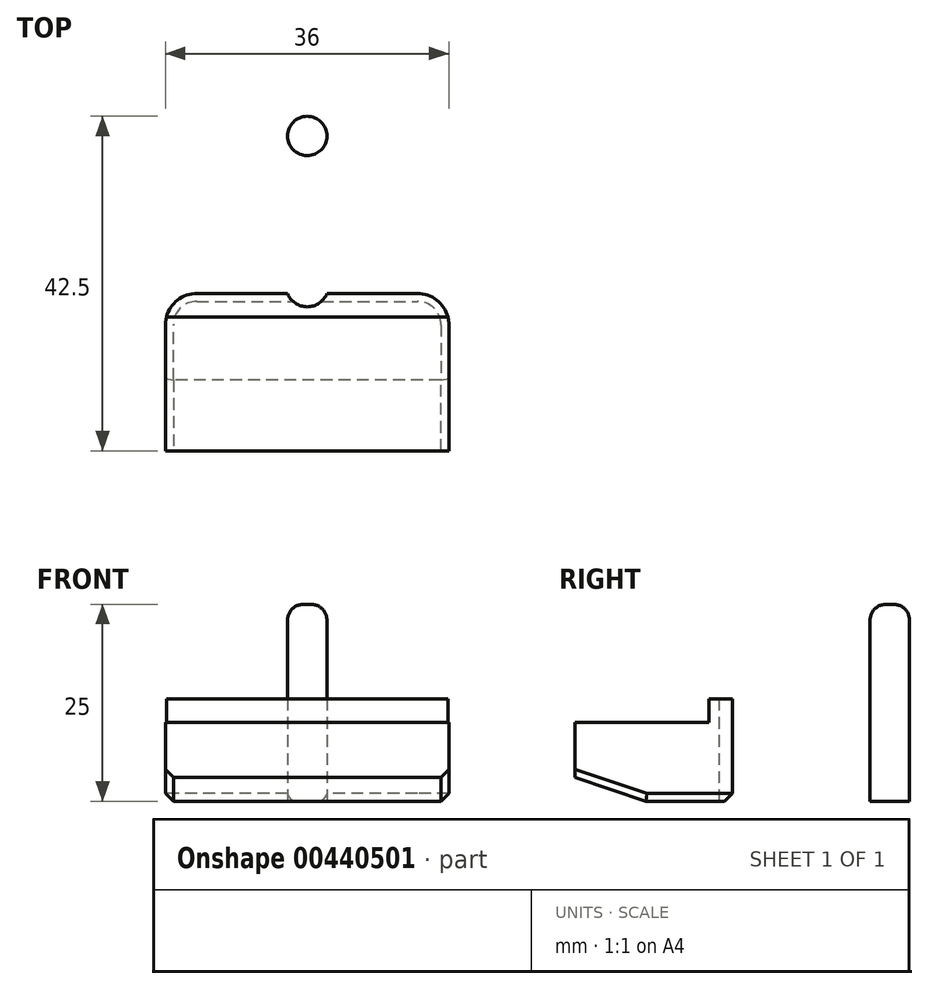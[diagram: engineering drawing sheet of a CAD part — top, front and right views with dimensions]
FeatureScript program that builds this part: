
annotation { "Feature Type Name" : "Feature", "Feature Type Description" : "" }
export const myFeature = defineFeature(function(context is Context, id is Id, definition is map)
    precondition{}
    {
        {
            var Q0;
            Q0=qCreatedBy(makeId("Top.planeOp"),FACE);
            var sketch = newSketch(context, id + "F0", { "sketchPlane" : qUnion([Q0])});
            skLineSegment(sketch, "E0.bottom", {"start": v(-18, 0) * mm, "end": v(18, 0) * mm});
            skLineSegment(sketch, "E0.top", {"start": v(-18, 20) * mm, "end": v(18, 20) * mm});
            skLineSegment(sketch, "E0.left", {"start": v(-18, 0) * mm, "end": v(-18, 20) * mm});
            skLineSegment(sketch, "E0.right", {"start": v(18, 0) * mm, "end": v(18, 20) * mm});
            skLineSegment(sketch, "E1.bottom", {"start": v(-10, 20) * mm, "end": v(10, 20) * mm});
            skLineSegment(sketch, "E1.top", {"start": v(-10, 50) * mm, "end": v(10, 50) * mm});
            skLineSegment(sketch, "E1.left", {"start": v(-10, 20) * mm, "end": v(-10, 50) * mm});
            skLineSegment(sketch, "E1.right", {"start": v(10, 20) * mm, "end": v(10, 50) * mm});
            skPoint(sketch, "E2", {"position": v(0, 21) * mm});
            skPoint(sketch, "E2.positionSnap0", {"position": v(0, 20) * mm});
            skPoint(sketch, "E3", {"position": v(0, 40) * mm});
            skCircle(sketch, "E4", {"center": v(0, 40) * mm, "radius": 2.5 * mm});
            skSolve(sketch);
        }
        {
            var Q0;
            Q0=makeQuery(id+"F0.imprint","IMPRINT",FACE,{"disambiguationData":[TD([[makeQuery(id+"F0.imprint","IMPRINT",EDGE,{"derivedFrom":sQuery(id+"F0.wireOp",EDGE,"E0.bottom")}),1.0]])]});
            var Q1;
            Q1=makeQuery(id+"F0.imprint","IMPRINT",FACE,{"disambiguationData":[TD([[makeQuery(id+"F0.imprint","IMPRINT",EDGE,{"derivedFrom":sQuery(id+"F0.wireOp",EDGE,"E1.bottom")}),1.0]])]});
            var Q2;
            Q2=makeQuery(id+"F0.imprint","IMPRINT",FACE,{"disambiguationData":[TD([[makeQuery(id+"F0.imprint","IMPRINT",EDGE,{"derivedFrom":sQuery(id+"F0.wireOp",EDGE,"E4")}),1.0]])]});
            extrude(context, id + "F1", {"entities" : qUnion([Q0, Q1, Q2]), "depth" : 13 * mm});
        }
        {
            var Q0;
            Q0=makeQuery(id+"F1.opExtrude","CAP_FACE",FACE,{"disambiguationData":[OSD([sQuery(id+"F0.wireOp",EDGE,"E0.bottom"),sQuery(id+"F0.wireOp",EDGE,"E0.top"),sQuery(id+"F0.wireOp",EDGE,"E0.left"),sQuery(id+"F0.wireOp",EDGE,"E0.right"),sQuery(id+"F0.wireOp",EDGE,"E1.top"),sQuery(id+"F0.wireOp",EDGE,"E1.left"),sQuery(id+"F0.wireOp",EDGE,"E1.right")])],"isStart":false});
            var sketch = newSketch(context, id + "F2", { "sketchPlane" : qUnion([Q0])});
            skLineSegment(sketch, "E5.bottom", {"start": v(-18, 0) * mm, "end": v(18, 0) * mm});
            skLineSegment(sketch, "E5.top", {"start": v(-18, 17) * mm, "end": v(18, 17) * mm});
            skLineSegment(sketch, "E5.left", {"start": v(-18, 0) * mm, "end": v(-18, 17) * mm});
            skLineSegment(sketch, "E5.right", {"start": v(18, 0) * mm, "end": v(18, 17) * mm});
            skSolve(sketch);
        }
        {
            var Q0;
            Q0=makeQuery(id+"F2.imprint","IMPRINT",FACE,{"disambiguationData":[TD([[makeQuery(id+"F2.imprint","IMPRINT",EDGE,{"derivedFrom":sQuery(id+"F2.wireOp",EDGE,"E5.bottom")}),1.0]])]});
            extrude(context, id + "F3", {"entities" : qUnion([Q0]), "operationType" : NewBodyOperationType.REMOVE, "oppositeDirection" : true, "depth" : 3 * mm});
        }
        {
            var Q0;
            Q0=sQuery(id+"F0.wireOp",VERTEX,"E2");
            var Q1;
            Q1=makeQuery(id+"F1.opExtrude","SWEPT_BODY",BODY,{"disambiguationData":[OSD([sQuery(id+"F0.wireOp",EDGE,"E0.bottom"),sQuery(id+"F0.wireOp",EDGE,"E0.top"),sQuery(id+"F0.wireOp",EDGE,"E0.left"),sQuery(id+"F0.wireOp",EDGE,"E0.right"),sQuery(id+"F0.wireOp",EDGE,"E1.top"),sQuery(id+"F0.wireOp",EDGE,"E1.left"),sQuery(id+"F0.wireOp",EDGE,"E1.right")])]});
            hole(context, id + "F4", {"style" : HoleStyle.SIMPLE, "endStyle" : HoleEndStyle.THROUGH, "oppositeDirection" : true, "holeDiameter" : 5.4 * mm, "isTappedThrough" : true, "tappedDepth" : 12 * mm, "tapClearance" : 3, "locations" : qUnion([Q0]), "scope" : qUnion([Q1])});
        }
        {
            var Q0;
            Q0=makeQuery(id+"F0.imprint","IMPRINT",FACE,{"disambiguationData":[TD([[makeQuery(id+"F0.imprint","IMPRINT",EDGE,{"derivedFrom":sQuery(id+"F0.wireOp",EDGE,"E4")}),1.0]])]});
            extrude(context, id + "F5", {"entities" : qUnion([Q0]), "operationType" : NewBodyOperationType.ADD, "depth" : 25 * mm});
        }
        {
            var Q0;
            Q0=makeQuery(id+"F5.opExtrude","CAP_EDGE",EDGE,{"disambiguationData":[OSD([sQuery(id+"F0.wireOp",EDGE,"E4")])],"isStart":false});
            fillet(context, id + "F6", {"entities" : qUnion([Q0]), "radius" : 2 * mm, "tangentPropagation" : true, "allowEdgeOverflow" : false});
        }
        {
            var Q0;
            Q0=makeQuery(id+"F1.opExtrude","SWEPT_EDGE",EDGE,{"disambiguationData":[OSD([sQuery(id+"F0.wireOp",EDGE,"E0.top"),sQuery(id+"F0.wireOp",EDGE,"E0.left")])]});
            var Q1;
            Q1=makeQuery(id+"F1.opExtrude","SWEPT_EDGE",EDGE,{"disambiguationData":[OSD([sQuery(id+"F0.wireOp",EDGE,"E0.top"),sQuery(id+"F0.wireOp",EDGE,"E0.right")])]});
            var Q2;
            Q2=makeQuery(id+"F1.opExtrude","SWEPT_EDGE",EDGE,{"disambiguationData":[OSD([sQuery(id+"F0.wireOp",EDGE,"E0.top"),sQuery(id+"F0.wireOp",EDGE,"E1.bottom"),sQuery(id+"F0.wireOp",EDGE,"E1.left")])]});
            var Q3;
            Q3=makeQuery(id+"F1.opExtrude","SWEPT_EDGE",EDGE,{"disambiguationData":[OSD([sQuery(id+"F0.wireOp",EDGE,"E0.top"),sQuery(id+"F0.wireOp",EDGE,"E1.bottom"),sQuery(id+"F0.wireOp",EDGE,"E1.right")])]});
            fillet(context, id + "F7", {"entities" : qUnion([Q0, Q1, Q2, Q3]), "radius" : 4 * mm, "tangentPropagation" : true, "allowEdgeOverflow" : false});
        }
        {
            var Q0;
            Q0=makeQuery(id+"F1.opExtrude","CAP_EDGE",EDGE,{"disambiguationData":[OSD([sQuery(id+"F0.wireOp",EDGE,"E1.top")])],"isStart":true});
            var Q1;
            Q1=makeQuery(id+"F1.opExtrude","CAP_EDGE",EDGE,{"disambiguationData":[OSD([sQuery(id+"F0.wireOp",EDGE,"E0.bottom")])],"isStart":true});
            chamfer(context, id + "F8", {"entities" : qUnion([Q0, Q1]), "chamferType" : ChamferType.TWO_OFFSETS, "width1" : 3 * mm, "oppositeDirection" : false, "width2" : 9 * mm, "tangentPropagation" : true});
        }
        {
            var Q0;
            {var subQ0=sQuery(id+"F0.wireOp",EDGE,"E0.right");var subQ1=sQuery(id+"F0.wireOp",EDGE,"E0.top");Q0=makeQuery(id+"F7.opFillet","BLEND_EDGE",EDGE,{"blendedFrom":[makeQuery(id+"F1.opExtrude","SWEPT_EDGE",EDGE,{"disambiguationData":[OSD([subQ1,subQ0])]}),makeQuery(id+"F1.opExtrude","CAP_FACE",FACE,{"disambiguationData":[OSD([sQuery(id+"F0.wireOp",EDGE,"E0.bottom"),subQ1,sQuery(id+"F0.wireOp",EDGE,"E0.left"),subQ0,sQuery(id+"F0.wireOp",EDGE,"E1.top"),sQuery(id+"F0.wireOp",EDGE,"E1.left"),sQuery(id+"F0.wireOp",EDGE,"E1.right")])],"isStart":true})],"blendedInto":[makeQuery(id+"F1.opExtrude","CAP_FACE",FACE,{"disambiguationData":[OSD([sQuery(id+"F0.wireOp",EDGE,"E0.bottom"),subQ1,sQuery(id+"F0.wireOp",EDGE,"E0.left"),subQ0,sQuery(id+"F0.wireOp",EDGE,"E1.top"),sQuery(id+"F0.wireOp",EDGE,"E1.left"),sQuery(id+"F0.wireOp",EDGE,"E1.right")])],"isStart":true})]});}
            var Q1;
            {var subQ0=sQuery(id+"F0.wireOp",EDGE,"E1.right");var subQ1=sQuery(id+"F0.wireOp",EDGE,"E0.top");Q1=makeQuery(id+"F7.opFillet","BLEND_EDGE",EDGE,{"blendedFrom":[makeQuery(id+"F1.opExtrude","SWEPT_EDGE",EDGE,{"disambiguationData":[OSD([subQ1,sQuery(id+"F0.wireOp",EDGE,"E1.bottom"),subQ0])]}),makeQuery(id+"F1.opExtrude","CAP_FACE",FACE,{"disambiguationData":[OSD([sQuery(id+"F0.wireOp",EDGE,"E0.bottom"),subQ1,sQuery(id+"F0.wireOp",EDGE,"E0.left"),sQuery(id+"F0.wireOp",EDGE,"E0.right"),sQuery(id+"F0.wireOp",EDGE,"E1.top"),sQuery(id+"F0.wireOp",EDGE,"E1.left"),subQ0])],"isStart":true})],"blendedInto":[makeQuery(id+"F1.opExtrude","CAP_FACE",FACE,{"disambiguationData":[OSD([sQuery(id+"F0.wireOp",EDGE,"E0.bottom"),subQ1,sQuery(id+"F0.wireOp",EDGE,"E0.left"),sQuery(id+"F0.wireOp",EDGE,"E0.right"),sQuery(id+"F0.wireOp",EDGE,"E1.top"),sQuery(id+"F0.wireOp",EDGE,"E1.left"),subQ0])],"isStart":true})]});}
            var Q2;
            {var subQ0=sQuery(id+"F0.wireOp",EDGE,"E1.left");var subQ1=sQuery(id+"F0.wireOp",EDGE,"E0.top");Q2=makeQuery(id+"F7.opFillet","BLEND_EDGE",EDGE,{"blendedFrom":[makeQuery(id+"F1.opExtrude","SWEPT_EDGE",EDGE,{"disambiguationData":[OSD([subQ1,sQuery(id+"F0.wireOp",EDGE,"E1.bottom"),subQ0])]}),makeQuery(id+"F1.opExtrude","CAP_FACE",FACE,{"disambiguationData":[OSD([sQuery(id+"F0.wireOp",EDGE,"E0.bottom"),subQ1,sQuery(id+"F0.wireOp",EDGE,"E0.left"),sQuery(id+"F0.wireOp",EDGE,"E0.right"),sQuery(id+"F0.wireOp",EDGE,"E1.top"),subQ0,sQuery(id+"F0.wireOp",EDGE,"E1.right")])],"isStart":true})],"blendedInto":[makeQuery(id+"F1.opExtrude","CAP_FACE",FACE,{"disambiguationData":[OSD([sQuery(id+"F0.wireOp",EDGE,"E0.bottom"),subQ1,sQuery(id+"F0.wireOp",EDGE,"E0.left"),sQuery(id+"F0.wireOp",EDGE,"E0.right"),sQuery(id+"F0.wireOp",EDGE,"E1.top"),subQ0,sQuery(id+"F0.wireOp",EDGE,"E1.right")])],"isStart":true})]});}
            var Q3;
            {var subQ0=sQuery(id+"F0.wireOp",EDGE,"E0.left");var subQ1=sQuery(id+"F0.wireOp",EDGE,"E0.top");Q3=makeQuery(id+"F7.opFillet","BLEND_EDGE",EDGE,{"blendedFrom":[makeQuery(id+"F1.opExtrude","SWEPT_EDGE",EDGE,{"disambiguationData":[OSD([subQ1,subQ0])]}),makeQuery(id+"F1.opExtrude","CAP_FACE",FACE,{"disambiguationData":[OSD([sQuery(id+"F0.wireOp",EDGE,"E0.bottom"),subQ1,subQ0,sQuery(id+"F0.wireOp",EDGE,"E0.right"),sQuery(id+"F0.wireOp",EDGE,"E1.top"),sQuery(id+"F0.wireOp",EDGE,"E1.left"),sQuery(id+"F0.wireOp",EDGE,"E1.right")])],"isStart":true})],"blendedInto":[makeQuery(id+"F1.opExtrude","CAP_FACE",FACE,{"disambiguationData":[OSD([sQuery(id+"F0.wireOp",EDGE,"E0.bottom"),subQ1,subQ0,sQuery(id+"F0.wireOp",EDGE,"E0.right"),sQuery(id+"F0.wireOp",EDGE,"E1.top"),sQuery(id+"F0.wireOp",EDGE,"E1.left"),sQuery(id+"F0.wireOp",EDGE,"E1.right")])],"isStart":true})]});}
            var Q4;
            Q4=makeQuery(id+"F8.opChamfer","BLEND_EDGE",EDGE,{"blendedFrom":[makeQuery(id+"F1.opExtrude","CAP_EDGE",EDGE,{"disambiguationData":[OSD([sQuery(id+"F0.wireOp",EDGE,"E0.bottom")])],"isStart":true}),makeQuery(id+"F1.opExtrude","SWEPT_FACE",FACE,{"disambiguationData":[OSD([sQuery(id+"F0.wireOp",EDGE,"E0.right")])]})],"blendedInto":[makeQuery(id+"F1.opExtrude","SWEPT_FACE",FACE,{"disambiguationData":[OSD([sQuery(id+"F0.wireOp",EDGE,"E0.right")])]})]});
            var Q5;
            Q5=makeQuery(id+"F8.opChamfer","BLEND_EDGE",EDGE,{"blendedFrom":[makeQuery(id+"F1.opExtrude","CAP_EDGE",EDGE,{"disambiguationData":[OSD([sQuery(id+"F0.wireOp",EDGE,"E0.bottom")])],"isStart":true}),makeQuery(id+"F1.opExtrude","SWEPT_FACE",FACE,{"disambiguationData":[OSD([sQuery(id+"F0.wireOp",EDGE,"E0.left")])]})],"blendedInto":[makeQuery(id+"F1.opExtrude","SWEPT_FACE",FACE,{"disambiguationData":[OSD([sQuery(id+"F0.wireOp",EDGE,"E0.left")])]})]});
            var Q6;
            Q6=makeQuery(id+"F1.opExtrude","SWEPT_EDGE",EDGE,{"disambiguationData":[OSD([sQuery(id+"F0.wireOp",EDGE,"E1.top"),sQuery(id+"F0.wireOp",EDGE,"E1.left")])]});
            var Q7;
            Q7=makeQuery(id+"F8.opChamfer","BLEND_EDGE",EDGE,{"blendedFrom":[makeQuery(id+"F1.opExtrude","CAP_EDGE",EDGE,{"disambiguationData":[OSD([sQuery(id+"F0.wireOp",EDGE,"E1.top")])],"isStart":true}),makeQuery(id+"F1.opExtrude","SWEPT_FACE",FACE,{"disambiguationData":[OSD([sQuery(id+"F0.wireOp",EDGE,"E1.left")])]})],"blendedInto":[makeQuery(id+"F1.opExtrude","SWEPT_FACE",FACE,{"disambiguationData":[OSD([sQuery(id+"F0.wireOp",EDGE,"E1.left")])]})]});
            var Q8;
            Q8=makeQuery(id+"F1.opExtrude","SWEPT_EDGE",EDGE,{"disambiguationData":[OSD([sQuery(id+"F0.wireOp",EDGE,"E1.top"),sQuery(id+"F0.wireOp",EDGE,"E1.right")])]});
            var Q9;
            Q9=makeQuery(id+"F8.opChamfer","BLEND_EDGE",EDGE,{"blendedFrom":[makeQuery(id+"F1.opExtrude","CAP_EDGE",EDGE,{"disambiguationData":[OSD([sQuery(id+"F0.wireOp",EDGE,"E1.top")])],"isStart":true}),makeQuery(id+"F1.opExtrude","SWEPT_FACE",FACE,{"disambiguationData":[OSD([sQuery(id+"F0.wireOp",EDGE,"E1.right")])]})],"blendedInto":[makeQuery(id+"F1.opExtrude","SWEPT_FACE",FACE,{"disambiguationData":[OSD([sQuery(id+"F0.wireOp",EDGE,"E1.right")])]})]});
            chamfer(context, id + "F9", {"entities" : qUnion([Q0, Q1, Q2, Q3, Q4, Q5, Q6, Q7, Q8, Q9]), "width" : 1 * mm, "tangentPropagation" : true});
        }
    });
